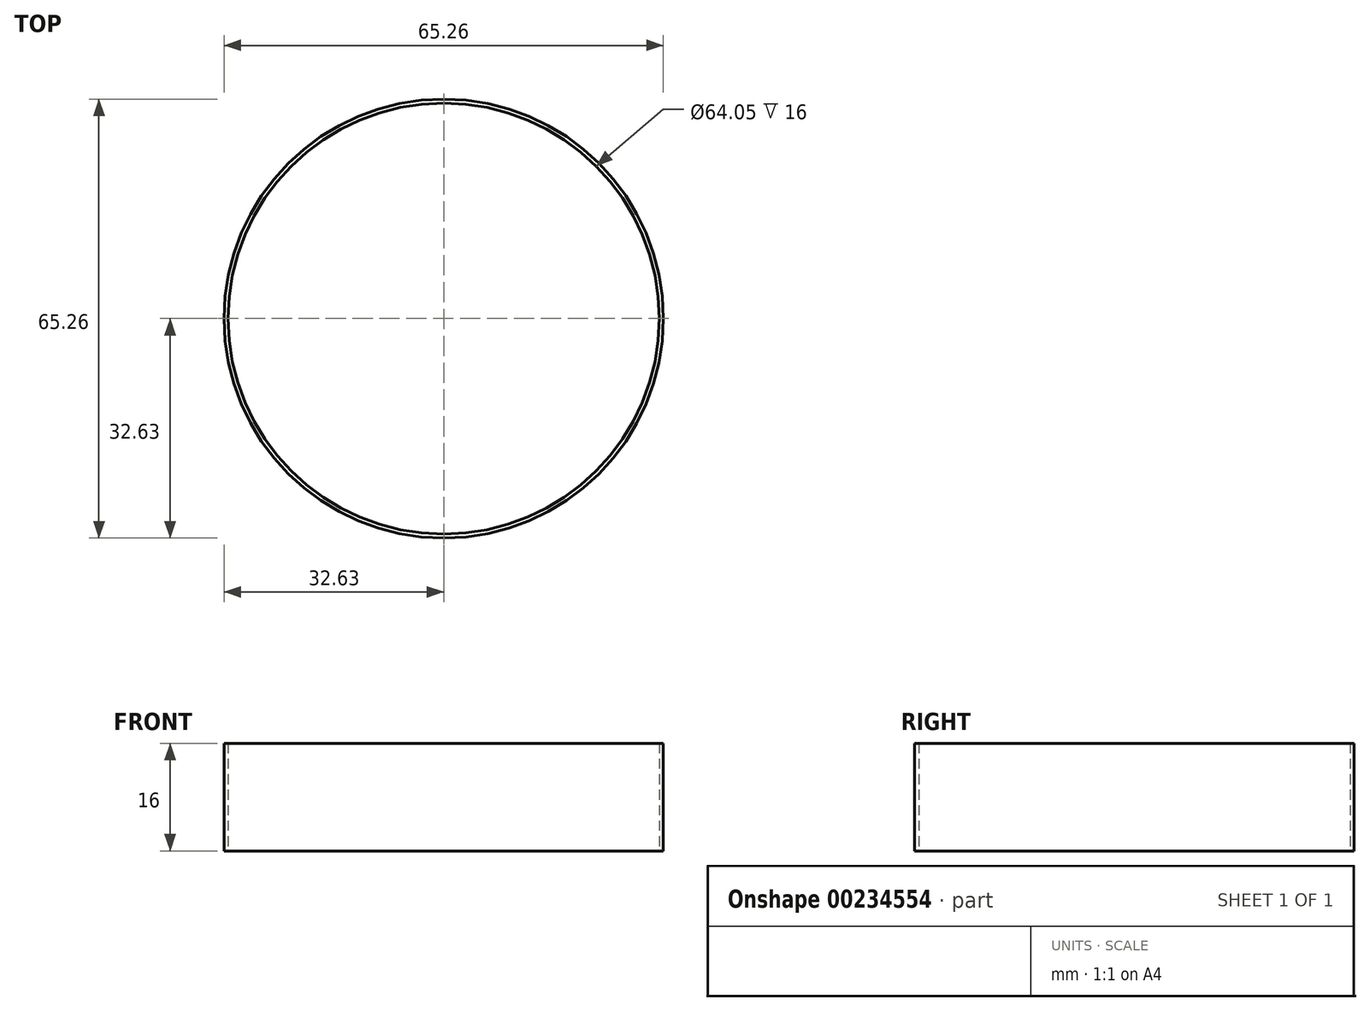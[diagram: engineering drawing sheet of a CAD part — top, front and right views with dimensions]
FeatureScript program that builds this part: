
annotation { "Feature Type Name" : "Feature", "Feature Type Description" : "" }
export const myFeature = defineFeature(function(context is Context, id is Id, definition is map)
    precondition{}
    {
        {
            var Q0;
            Q0=qCreatedBy(makeId("Top.planeOp"),FACE);
            var sketch = newSketch(context, id + "F0", { "sketchPlane" : qUnion([Q0])});
            skArc(sketch, "E0", {"start": v(-32.62, 0) * mm, "mid": v(-12.49, -30.14) * mm, "end": v(23.07, -23.07) * mm});
            skLineSegment(sketch, "E1", {"start": v(0, 32.62) * mm, "end": v(0, -32.62) * mm, "construction": true});
            skLineSegment(sketch, "E2", {"start": v(32.62, 0) * mm, "end": v(-32.62, 0) * mm, "construction": true});
            skLineSegment(sketch, "E3", {"start": v(-23.07, 23.07) * mm, "end": v(23.07, -23.07) * mm, "construction": true});
            skLineSegment(sketch, "E4", {"start": v(23.07, 23.07) * mm, "end": v(-23.07, -23.07) * mm, "construction": true});
            skArc(sketch, "E5", {"start": v(-23.07, 23.07) * mm, "mid": v(-30.14, 12.49) * mm, "end": v(-32.62, 0) * mm});
            skArc(sketch, "E6.trimOffspring", {"start": v(32.62, 0) * mm, "mid": v(12.49, 30.14) * mm, "end": v(-23.07, 23.07) * mm});
            skArc(sketch, "E7", {"start": v(23.07, -23.07) * mm, "mid": v(30.14, -12.49) * mm, "end": v(32.62, 0) * mm});
            skArc(sketch, "E8.0", {"start": v(32.02, 0) * mm, "mid": v(12.26, 29.59) * mm, "end": v(-22.65, 22.65) * mm});
            skArc(sketch, "E8.1", {"start": v(22.65, -22.65) * mm, "mid": v(29.59, -12.26) * mm, "end": v(32.02, 0) * mm});
            skArc(sketch, "E8.2", {"start": v(-32.02, 0) * mm, "mid": v(-12.26, -29.59) * mm, "end": v(22.65, -22.65) * mm});
            skArc(sketch, "E8.3", {"start": v(-22.65, 22.65) * mm, "mid": v(-29.59, 12.26) * mm, "end": v(-32.02, 0) * mm});
            skSolve(sketch);
        }
        {
            var Q0;
            Q0=makeQuery(id+"F0.imprint","IMPRINT",FACE,{"disambiguationData":[TD([[makeQuery(id+"F0.imprint","IMPRINT",EDGE,{"derivedFrom":sQuery(id+"F0.wireOp",EDGE,"E0")}),1.0]])]});
            extrude(context, id + "F1", {"entities" : qUnion([Q0]), "depth" : 16 * mm});
        }
    });
